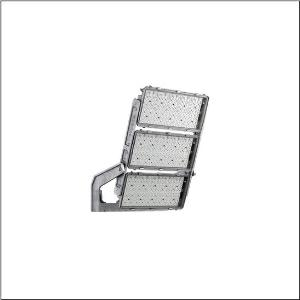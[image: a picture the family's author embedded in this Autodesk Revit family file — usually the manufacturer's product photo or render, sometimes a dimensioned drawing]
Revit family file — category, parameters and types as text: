
# Revit family: floodlight_fl_11_maxi_pro_remote___pl33t_5xa779426t01aa_e8f6
name_source: partatom
category: Lighting Fixtures
units: mm (PartAtom-declared; Revit-internal decimal feet)

## family parameters
Cut with Voids When Loaded = No
Host = Face
Light Source = No
Part Type = Normal
Room Calculation Point = No
Round Connector Dimension = Use Diameter
Shared = No

## types (1)
- --- (1 x LED, 211660 lm, 1539.7 W, 4000K)
    Apparent Load = 1540 VA
    CIE Flux Codes = 27 70 98 100 100
    Color Rendering = 70
    Color Temperature = 4000K
    Default Elevation = 1800 mm
    Description = Floodlight FL 11  maxi  pro Remote floodlight; light control with lens of PMMA; cover panel of toughened safety glass, transparent; light distribution: PL33T, asymmetric direct distribution, LEDcolour temperature: 4000K, rated luminous flux: 211.660lm, colour rendering: CRI > 70, light colour: 740; luminous efficacy: 138lm/W; brightness control: DALI 2 (1 DALI address); with terminal, 8-pole, max. 2.5mm², mains connection: 220..240V/380..400V AC, 50/60Hz, surge voltage resistance: line to ground: 10kV, ECG replaceable separately, no afterglow with DALI off / DMX off command, LED unit replaceable without ESD environment, dustproof LED module, dimming range 10..100%; 1540W floodlight with 2x LED unit of diecast aluminium, coated grey; length: 713mm / width: 651mm / height: 338mm; mounting bracket, of diecast aluminium, uncoated, natural, equipment: Power, protection rating (complete): IP66; insulation class (complete): insulation class I (protective earthing); certification: CE, ENEC, VDE; ball protection: ball impact resistance with accessories, impact resistance: IK07; only for outdoor installations, rated ambient temperature 10°C, permissible operating ambient temperature: -40..+30°C, permissible storage temperature: -40..+85°C; packaging unit: 1 piece

Light Distribution: PL33T
    Height = 320 mm
    Lamp = 1 x LED
    Lamp Light Flux = 211660 lm
    Lamp Power = 1539.7 W
    Lamp count = 1
    Length = 1002 mm
    Luminous efficacy = 137 lm/W
    Manufacturer = Siteco
    ModVariant = No
    Model = 5XA779426T01AA
    Mounting Place = Ceiling
    Mounting Type = Surface mounted
    Number of Poles = 1
    OnlyDefault = Yes
    Power Factor = 1
    Product Name = Floodlight FL 11 maxi pro Remote | PL33T
    Product group = floodlight | ceiling mounted
    ProductGroupID = 303
    Protection Class = Protection class I
    Protection Degree = IP 66
    RLX_Detail_Level = 1
    RLX_Emergency_Light_Flux = 0 lm
    RLX_Emergency_Type = 0
    RLX_Emergency_Type_DB = No
    RlxData = <blob elided: 52377 chars, md5=b0c0706f>
    Socket = socket
    Standby Power = 0 W
    System Light Flux = 211660 lm
    System Power = 1540 W
    Type Comments = factory setting: luminous flux: 100 % | dim-lin: 254 | 1080 mA
    Type Image = l_1006784.jpg
    URL = http://relux.com
    VarID = @adj_030707
    Voltage = 0 V
    Weight = 0.00 kg
    Width = 655 mm

## geometry (parser evidence)
native form markers: Blend x4, Sweep x14
no freeform markers — native parametric forms only
